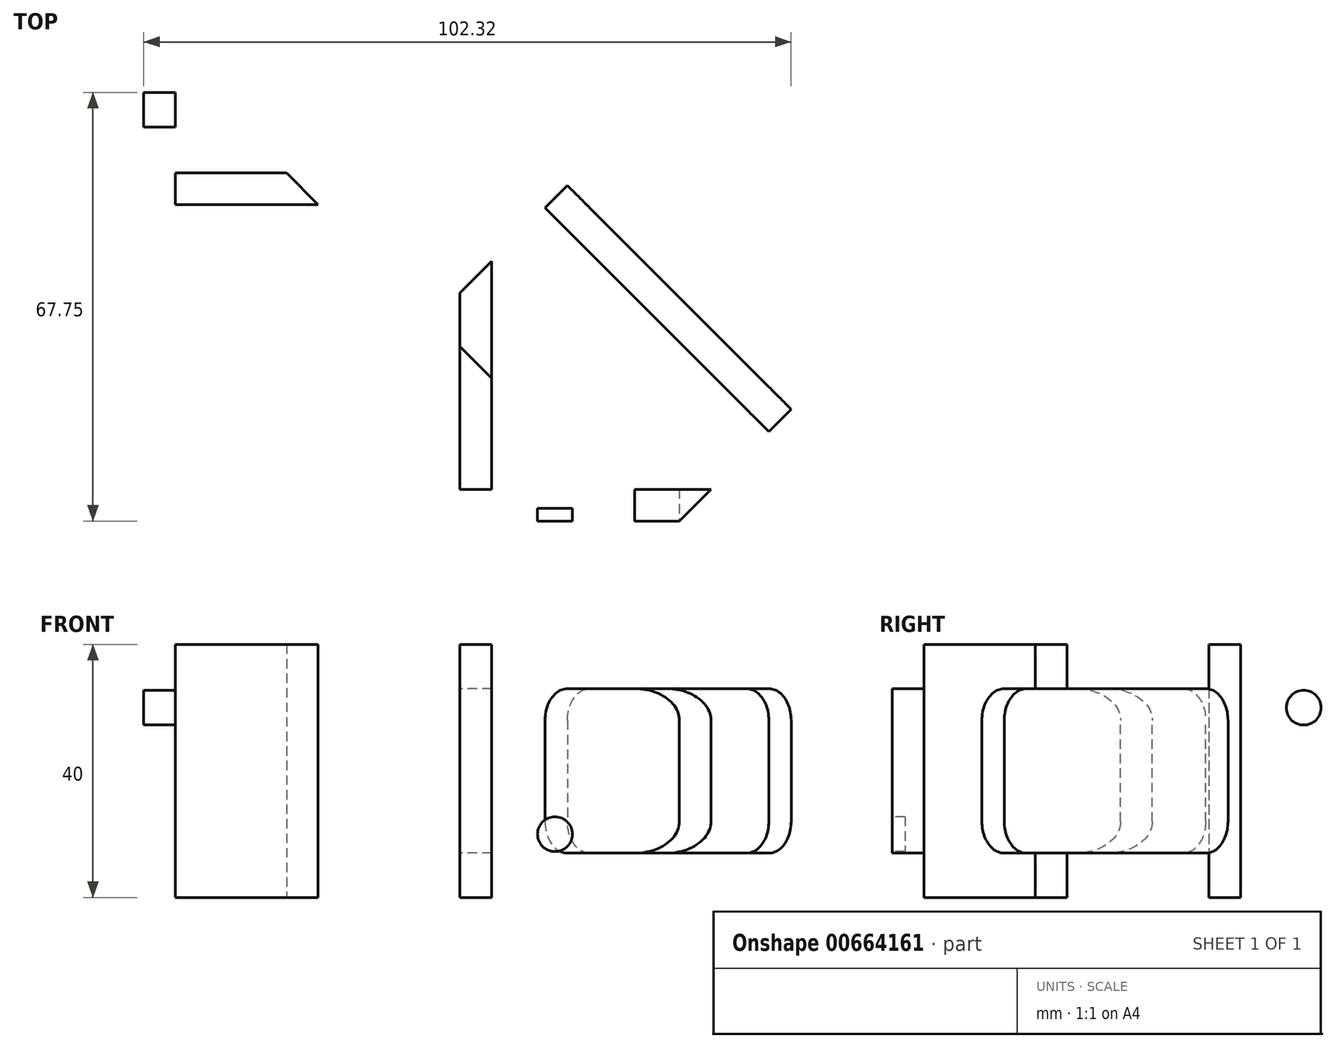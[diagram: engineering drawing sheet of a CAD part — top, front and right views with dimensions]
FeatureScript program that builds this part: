
annotation { "Feature Type Name" : "Feature", "Feature Type Description" : "" }
export const myFeature = defineFeature(function(context is Context, id is Id, definition is map)
    precondition{}
    {
        {
            var Q0;
            Q0=qCreatedBy(makeId("Top.planeOp"),FACE);
            var sketch = newSketch(context, id + "F0", { "sketchPlane" : qUnion([Q0])});
            skLineSegment(sketch, "E0", {"start": v(0, 120) * mm, "end": v(0, 0) * mm});
            skLineSegment(sketch, "E1", {"start": v(0, 0) * mm, "end": v(120, 0) * mm});
            skLineSegment(sketch, "E2", {"start": v(120, 0) * mm, "end": v(0, 120) * mm});
            skLineSegment(sketch, "E3.bottom", {"start": v(0, 0) * mm, "end": v(50, 0) * mm});
            skLineSegment(sketch, "E3.top", {"start": v(0, 50) * mm, "end": v(50, 50) * mm});
            skLineSegment(sketch, "E3.left", {"start": v(0, 0) * mm, "end": v(0, 50) * mm});
            skLineSegment(sketch, "E3.right", {"start": v(50, 0) * mm, "end": v(50, 50) * mm});
            skLineSegment(sketch, "E4", {"start": v(0, 100) * mm, "end": v(100, 0) * mm});
            skLineSegment(sketch, "E5", {"start": v(0, 92.93) * mm, "end": v(42.93, 50) * mm});
            skLineSegment(sketch, "E6", {"start": v(50, 42.93) * mm, "end": v(92.93, 0) * mm});
            skSolve(sketch);
        }
        {
            var Q0;
            {var subQ0=sQuery(id+"F0.wireOp",EDGE,"E0");Q0=makeQuery(id+"F0.imprint","IMPRINT",FACE,{"disambiguationData":[TD([[makeQuery(id+"F0.imprint","IMPRINT",EDGE,{"derivedFrom":subQ0}),1.0]])]});}
            var Q1;
            {var subQ0=sQuery(id+"F0.wireOp",EDGE,"RjJmAIRv-SbMF-DeTt-ittY-7XkKLRqEJTLq");Q1=makeQuery(id+"F0.imprint","IMPRINT",FACE,{"disambiguationData":[TD([[makeQuery(id+"F0.imprint","IMPRINT",EDGE,{"derivedFrom":subQ0}),-1.0]])]});}
            var Q2;
            {var subQ0=sQuery(id+"F0.wireOp",EDGE,"E1");Q2=makeQuery(id+"F0.imprint","IMPRINT",FACE,{"disambiguationData":[TD([[makeQuery(id+"F0.imprint","IMPRINT",EDGE,{"derivedFrom":subQ0}),1.0]])]});}
            var Q3;
            {var subQ3=sQuery(id+"F0.wireOp",EDGE,"E5");Q3=makeQuery(id+"F0.imprint","IMPRINT",FACE,{"disambiguationData":[TD([[makeQuery(id+"F0.imprint","IMPRINT",EDGE,{"derivedFrom":subQ3}),1.0]])]});}
            var Q4;
            {var subQ3=sQuery(id+"F0.wireOp",EDGE,"E6");Q4=makeQuery(id+"F0.imprint","IMPRINT",FACE,{"disambiguationData":[TD([[makeQuery(id+"F0.imprint","IMPRINT",EDGE,{"derivedFrom":subQ3}),1.0]])]});}
            var Q5;
            {var subQ4=sQuery(id+"F0.wireOp",EDGE,"E2");Q5=makeQuery(id+"F0.imprint","IMPRINT",FACE,{"disambiguationData":[TD([[makeQuery(id+"F0.imprint","IMPRINT",EDGE,{"derivedFrom":subQ4}),1.0]])]});}
            extrude(context, id + "F1", {"entities" : qUnion([Q0, Q1, Q2, Q3, Q4, Q5]), "depth" : 40 * mm, "offsetDistance" : 25 * mm});
        }
        {
            var Q0;
            Q0=makeQuery(id+"F1.opExtrude","CAP_FACE",FACE,{"disambiguationData":[OSD([sQuery(id+"F0.wireOp",EDGE,"E0"),sQuery(id+"F0.wireOp",EDGE,"E1"),sQuery(id+"F0.wireOp",EDGE,"E2"),sQuery(id+"F0.wireOp",EDGE,"E3.top"),sQuery(id+"F0.wireOp",EDGE,"E3.right")])],"isStart":false});
            var Q1;
            Q1=makeQuery(id+"F1.opExtrude","CAP_FACE",FACE,{"disambiguationData":[OSD([sQuery(id+"F0.wireOp",EDGE,"E0"),sQuery(id+"F0.wireOp",EDGE,"E1"),sQuery(id+"F0.wireOp",EDGE,"E2"),sQuery(id+"F0.wireOp",EDGE,"E3.top"),sQuery(id+"F0.wireOp",EDGE,"E3.right")])],"isStart":true});
            shell(context, id + "F2", {"entities" : qUnion([Q0, Q1]), "thickness" : 5 * mm});
        }
        {
            var Q0;
            Q0=makeQuery(id+"F1.opExtrude","SWEPT_FACE",FACE,{"disambiguationData":[OSD([sQuery(id+"F0.wireOp",EDGE,"E2")])]});
            var sketch = newSketch(context, id + "F3", { "sketchPlane" : qUnion([Q0])});
            skLineSegment(sketch, "E7.bottom", {"start": v(54.85, 33) * mm, "end": v(14.85, 33) * mm});
            skLineSegment(sketch, "E7.top", {"start": v(54.85, 7) * mm, "end": v(14.85, 7) * mm});
            skLineSegment(sketch, "E7.left", {"start": v(59.85, 28) * mm, "end": v(59.85, 12) * mm});
            skLineSegment(sketch, "E7.right", {"start": v(9.85, 28) * mm, "end": v(9.85, 12) * mm});
            skPoint(sketch, "E8.visualSharp", {"position": v(9.85, 33) * mm});
            skArc(sketch, "E8.filletArc", {"start": v(14.85, 33) * mm, "mid": v(11.32, 31.54) * mm, "end": v(9.85, 28) * mm});
            skPoint(sketch, "E9.visualSharp", {"position": v(9.85, 7) * mm});
            skArc(sketch, "E9.filletArc", {"start": v(9.85, 12) * mm, "mid": v(11.32, 8.46) * mm, "end": v(14.85, 7) * mm});
            skPoint(sketch, "E10.visualSharp", {"position": v(59.85, 33) * mm});
            skArc(sketch, "E10.filletArc", {"start": v(59.85, 28) * mm, "mid": v(58.39, 31.54) * mm, "end": v(54.85, 33) * mm});
            skPoint(sketch, "E11.visualSharp", {"position": v(59.85, 7) * mm});
            skArc(sketch, "E11.filletArc", {"start": v(54.85, 7) * mm, "mid": v(58.39, 8.46) * mm, "end": v(59.85, 12) * mm});
            skLineSegment(sketch, "E12", {"start": v(0, 40) * mm, "end": v(0, 0) * mm, "construction": true});
            skArc(sketch, "E13.MirrorCS", {"start": v(-59.85, 28) * mm, "mid": v(-58.39, 31.54) * mm, "end": v(-54.85, 33) * mm});
            skArc(sketch, "E14.MirrorCS", {"start": v(-54.85, 7) * mm, "mid": v(-58.39, 8.46) * mm, "end": v(-59.85, 12) * mm});
            skLineSegment(sketch, "E15.MirrorCS", {"start": v(-59.85, 28) * mm, "end": v(-59.85, 12) * mm});
            skPoint(sketch, "E16.MirrorP", {"position": v(-59.85, 7) * mm});
            skPoint(sketch, "E17.MirrorP", {"position": v(-59.85, 33) * mm});
            skArc(sketch, "E18.MirrorCS", {"start": v(-14.85, 33) * mm, "mid": v(-11.32, 31.54) * mm, "end": v(-9.85, 28) * mm});
            skPoint(sketch, "E19.MirrorP", {"position": v(-9.85, 33) * mm});
            skArc(sketch, "E20.MirrorCS", {"start": v(-9.85, 12) * mm, "mid": v(-11.32, 8.46) * mm, "end": v(-14.85, 7) * mm});
            skLineSegment(sketch, "E21.MirrorCS", {"start": v(-54.85, 33) * mm, "end": v(-14.85, 33) * mm});
            skLineSegment(sketch, "E22.MirrorCS", {"start": v(-54.85, 7) * mm, "end": v(-14.85, 7) * mm});
            skLineSegment(sketch, "E23.MirrorCS", {"start": v(-9.85, 28) * mm, "end": v(-9.85, 12) * mm});
            skPoint(sketch, "E24.MirrorP", {"position": v(-9.85, 7) * mm});
            skSolve(sketch);
        }
        {
            var Q0;
            Q0=makeQuery(id+"F3.imprint","IMPRINT",FACE,{"disambiguationData":[TD([[makeQuery(id+"F3.imprint","IMPRINT",EDGE,{"derivedFrom":sQuery(id+"F3.wireOp",EDGE,"E7.bottom")}),1.0]])]});
            var Q1;
            Q1=makeQuery(id+"F3.imprint","IMPRINT",FACE,{"disambiguationData":[TD([[makeQuery(id+"F3.imprint","IMPRINT",EDGE,{"derivedFrom":sQuery(id+"F3.wireOp",EDGE,"E14.MirrorCS")}),-1.0]])]});
            extrude(context, id + "F4", {"entities" : qUnion([Q0, Q1]), "operationType" : NewBodyOperationType.REMOVE, "oppositeDirection" : true, "depth" : 30 * mm, "offsetDistance" : 25 * mm});
        }
        {
            var Q0;
            Q0=makeQuery(id+"F1.opExtrude","SWEPT_FACE",FACE,{"disambiguationData":[OSD([sQuery(id+"F0.wireOp",EDGE,"E0")])]});
            var sketch = newSketch(context, id + "F5", { "sketchPlane" : qUnion([Q0])});
            skCircle(sketch, "E25", {"center": v(-95, 10) * mm, "radius": 2.75 * mm});
            skCircle(sketch, "E26", {"center": v(-65, 10) * mm, "radius": 2.75 * mm});
            skLineSegment(sketch, "E27", {"start": v(-120, 20) * mm, "end": v(-50, 20) * mm, "construction": true});
            skCircle(sketch, "E28.MirrorC", {"center": v(-95, 30) * mm, "radius": 2.75 * mm});
            skCircle(sketch, "E29.MirrorC", {"center": v(-65, 30) * mm, "radius": 2.75 * mm});
            skSolve(sketch);
        }
        {
            var Q0;
            Q0=makeQuery(id+"F5.imprint","IMPRINT",FACE,{"disambiguationData":[TD([[makeQuery(id+"F5.imprint","IMPRINT",EDGE,{"derivedFrom":sQuery(id+"F5.wireOp",EDGE,"E25")}),1.0]])]});
            var Q1;
            Q1=makeQuery(id+"F5.imprint","IMPRINT",FACE,{"disambiguationData":[TD([[makeQuery(id+"F5.imprint","IMPRINT",EDGE,{"derivedFrom":sQuery(id+"F5.wireOp",EDGE,"E28.MirrorC")}),-1.0]])]});
            var Q2;
            Q2=makeQuery(id+"F5.imprint","IMPRINT",FACE,{"disambiguationData":[TD([[makeQuery(id+"F5.imprint","IMPRINT",EDGE,{"derivedFrom":sQuery(id+"F5.wireOp",EDGE,"E26")}),1.0]])]});
            var Q3;
            Q3=makeQuery(id+"F5.imprint","IMPRINT",FACE,{"disambiguationData":[TD([[makeQuery(id+"F5.imprint","IMPRINT",EDGE,{"derivedFrom":sQuery(id+"F5.wireOp",EDGE,"E29.MirrorC")}),-1.0]])]});
            var Q4;
            Q4=makeQuery(id+"F2.opShell","OFFSET_FACE",FACE,{"disambiguationData":[OSD([sQuery(id+"F0.wireOp",EDGE,"E0")])]});
            extrude(context, id + "F6", {"entities" : qUnion([Q0, Q1, Q2, Q3]), "operationType" : NewBodyOperationType.REMOVE, "endBound" : BoundingType.UP_TO_SURFACE, "oppositeDirection" : true, "depth" : 25 * mm, "endBoundEntityFace" : qUnion([Q4]), "offsetDistance" : 25 * mm});
        }
        {
            var Q0;
            Q0=makeQuery(id+"F1.opExtrude","SWEPT_FACE",FACE,{"disambiguationData":[OSD([sQuery(id+"F0.wireOp",EDGE,"E1")])]});
            var sketch = newSketch(context, id + "F7", { "sketchPlane" : qUnion([Q0])});
            skLineSegment(sketch, "E30", {"start": v(120, 20) * mm, "end": v(50, 20) * mm, "construction": true});
            skCircle(sketch, "E31", {"center": v(95, 30) * mm, "radius": 2.75 * mm});
            skCircle(sketch, "E32", {"center": v(65, 30) * mm, "radius": 2.75 * mm});
            skCircle(sketch, "E33.MirrorC", {"center": v(95, 10) * mm, "radius": 2.75 * mm});
            skCircle(sketch, "E34.MirrorC", {"center": v(65, 10) * mm, "radius": 2.75 * mm});
            skSolve(sketch);
        }
        {
            var Q0;
            Q0=makeQuery(id+"F7.imprint","IMPRINT",FACE,{"disambiguationData":[TD([[makeQuery(id+"F7.imprint","IMPRINT",EDGE,{"derivedFrom":sQuery(id+"F7.wireOp",EDGE,"E32")}),1.0]])]});
            var Q1;
            Q1=makeQuery(id+"F7.imprint","IMPRINT",FACE,{"disambiguationData":[TD([[makeQuery(id+"F7.imprint","IMPRINT",EDGE,{"derivedFrom":sQuery(id+"F7.wireOp",EDGE,"E31")}),1.0]])]});
            var Q2;
            Q2=makeQuery(id+"F7.imprint","IMPRINT",FACE,{"disambiguationData":[TD([[makeQuery(id+"F7.imprint","IMPRINT",EDGE,{"derivedFrom":sQuery(id+"F7.wireOp",EDGE,"E33.MirrorC")}),-1.0]])]});
            var Q3;
            Q3=makeQuery(id+"F7.imprint","IMPRINT",FACE,{"disambiguationData":[TD([[makeQuery(id+"F7.imprint","IMPRINT",EDGE,{"derivedFrom":sQuery(id+"F7.wireOp",EDGE,"E34.MirrorC")}),-1.0]])]});
            var Q4;
            Q4=makeQuery(id+"F2.opShell","OFFSET_FACE",FACE,{"disambiguationData":[OSD([sQuery(id+"F0.wireOp",EDGE,"E1")])]});
            extrude(context, id + "F8", {"entities" : qUnion([Q0, Q1, Q2, Q3]), "operationType" : NewBodyOperationType.REMOVE, "endBound" : BoundingType.UP_TO_SURFACE, "oppositeDirection" : true, "depth" : 25 * mm, "endBoundEntityFace" : qUnion([Q4]), "offsetDistance" : 25 * mm});
        }
        {
            var Q0;
            Q0=makeQuery(id+"F2.opShell","OFFSET_FACE",FACE,{"disambiguationData":[OSD([sQuery(id+"F0.wireOp",EDGE,"E0")])]});
            var sketch = newSketch(context, id + "F9", { "sketchPlane" : qUnion([Q0])});
            skCircle(sketch, "E35.cCircle", {"center": v(65, 30) * mm, "radius": 3.85 * mm, "construction": true});
            skLineSegment(sketch, "E35.0", {"start": v(65, 25.55) * mm, "end": v(61.15, 27.78) * mm});
            skLineSegment(sketch, "E35.1", {"start": v(61.15, 27.78) * mm, "end": v(61.15, 32.22) * mm});
            skLineSegment(sketch, "E35.2", {"start": v(61.15, 32.22) * mm, "end": v(65, 34.45) * mm});
            skLineSegment(sketch, "E35.3", {"start": v(65, 34.45) * mm, "end": v(68.85, 32.22) * mm});
            skLineSegment(sketch, "E35.4", {"start": v(68.85, 32.22) * mm, "end": v(68.85, 27.78) * mm});
            skLineSegment(sketch, "E35.5", {"start": v(68.85, 27.78) * mm, "end": v(65, 25.55) * mm});
            skPoint(sketch, "E35.0.midPoint", {"position": v(63.08, 26.67) * mm});
            skCircle(sketch, "E36.cCircle", {"center": v(65, 10) * mm, "radius": 3.85 * mm, "construction": true});
            skLineSegment(sketch, "E36.0", {"start": v(61.15, 7.78) * mm, "end": v(61.15, 12.22) * mm});
            skLineSegment(sketch, "E36.1", {"start": v(61.15, 12.22) * mm, "end": v(65, 14.45) * mm});
            skLineSegment(sketch, "E36.2", {"start": v(65, 14.45) * mm, "end": v(68.85, 12.22) * mm});
            skLineSegment(sketch, "E36.3", {"start": v(68.85, 12.22) * mm, "end": v(68.85, 7.78) * mm});
            skLineSegment(sketch, "E36.4", {"start": v(68.85, 7.78) * mm, "end": v(65, 5.55) * mm});
            skLineSegment(sketch, "E36.5", {"start": v(65, 5.55) * mm, "end": v(61.15, 7.78) * mm});
            skPoint(sketch, "E36.0.midPoint", {"position": v(61.15, 10) * mm});
            skCircle(sketch, "E37.cCircle", {"center": v(95, 30) * mm, "radius": 3.85 * mm, "construction": true});
            skLineSegment(sketch, "E37.0", {"start": v(95, 25.55) * mm, "end": v(91.15, 27.78) * mm});
            skLineSegment(sketch, "E37.1", {"start": v(91.15, 27.78) * mm, "end": v(91.15, 32.22) * mm});
            skLineSegment(sketch, "E37.2", {"start": v(91.15, 32.22) * mm, "end": v(95, 34.45) * mm});
            skLineSegment(sketch, "E37.3", {"start": v(95, 34.45) * mm, "end": v(98.85, 32.22) * mm});
            skLineSegment(sketch, "E37.4", {"start": v(98.85, 32.22) * mm, "end": v(98.85, 27.78) * mm});
            skLineSegment(sketch, "E37.5", {"start": v(98.85, 27.78) * mm, "end": v(95, 25.55) * mm});
            skPoint(sketch, "E37.0.midPoint", {"position": v(93.07, 26.67) * mm});
            skCircle(sketch, "E38.cCircle", {"center": v(95, 10) * mm, "radius": 3.85 * mm, "construction": true});
            skLineSegment(sketch, "E38.0", {"start": v(95, 5.55) * mm, "end": v(91.15, 7.78) * mm});
            skLineSegment(sketch, "E38.1", {"start": v(91.15, 7.78) * mm, "end": v(91.15, 12.22) * mm});
            skLineSegment(sketch, "E38.2", {"start": v(91.15, 12.22) * mm, "end": v(95, 14.45) * mm});
            skLineSegment(sketch, "E38.3", {"start": v(95, 14.45) * mm, "end": v(98.85, 12.22) * mm});
            skLineSegment(sketch, "E38.4", {"start": v(98.85, 12.22) * mm, "end": v(98.85, 7.78) * mm});
            skLineSegment(sketch, "E38.5", {"start": v(98.85, 7.78) * mm, "end": v(95, 5.55) * mm});
            skPoint(sketch, "E38.0.midPoint", {"position": v(93.08, 6.67) * mm});
            skSolve(sketch);
        }
        {
            var Q0;
            Q0=makeQuery(id+"F9.imprint","IMPRINT",FACE,{"disambiguationData":[TD([[makeQuery(id+"F9.imprint","IMPRINT",EDGE,{"derivedFrom":sQuery(id+"F9.wireOp",EDGE,"E35.0")}),-1.0]])]});
            var Q1;
            Q1=makeQuery(id+"F9.imprint","IMPRINT",FACE,{"disambiguationData":[TD([[makeQuery(id+"F9.imprint","IMPRINT",EDGE,{"derivedFrom":sQuery(id+"F9.wireOp",EDGE,"E36.0")}),-1.0]])]});
            var Q2;
            Q2=makeQuery(id+"F9.imprint","IMPRINT",FACE,{"disambiguationData":[TD([[makeQuery(id+"F9.imprint","IMPRINT",EDGE,{"derivedFrom":sQuery(id+"F9.wireOp",EDGE,"E38.0")}),-1.0]])]});
            var Q3;
            Q3=makeQuery(id+"F9.imprint","IMPRINT",FACE,{"disambiguationData":[TD([[makeQuery(id+"F9.imprint","IMPRINT",EDGE,{"derivedFrom":sQuery(id+"F9.wireOp",EDGE,"E37.0")}),-1.0]])]});
            extrude(context, id + "F10", {"entities" : qUnion([Q0, Q1, Q2, Q3]), "operationType" : NewBodyOperationType.REMOVE, "oppositeDirection" : true, "depth" : 3 * mm, "offsetDistance" : 25 * mm});
        }
        {
            var Q0;
            Q0=makeQuery(id+"F2.opShell","OFFSET_FACE",FACE,{"disambiguationData":[OSD([sQuery(id+"F0.wireOp",EDGE,"E1")])]});
            var sketch = newSketch(context, id + "F11", { "sketchPlane" : qUnion([Q0])});
            skCircle(sketch, "E39.cCircle", {"center": v(-95, 30) * mm, "radius": 3.85 * mm, "construction": true});
            skLineSegment(sketch, "E39.0", {"start": v(-95, 34.45) * mm, "end": v(-91.15, 32.22) * mm});
            skLineSegment(sketch, "E39.1", {"start": v(-91.15, 32.22) * mm, "end": v(-91.15, 27.78) * mm});
            skLineSegment(sketch, "E39.2", {"start": v(-91.15, 27.78) * mm, "end": v(-95, 25.55) * mm});
            skLineSegment(sketch, "E39.3", {"start": v(-95, 25.55) * mm, "end": v(-98.85, 27.78) * mm});
            skLineSegment(sketch, "E39.4", {"start": v(-98.85, 27.78) * mm, "end": v(-98.85, 32.22) * mm});
            skLineSegment(sketch, "E39.5", {"start": v(-98.85, 32.22) * mm, "end": v(-95, 34.45) * mm});
            skPoint(sketch, "E39.0.midPoint", {"position": v(-93.07, 33.33) * mm});
            skCircle(sketch, "E40.cCircle", {"center": v(-95, 10) * mm, "radius": 3.85 * mm, "construction": true});
            skLineSegment(sketch, "E40.0", {"start": v(-95, 14.45) * mm, "end": v(-91.15, 12.22) * mm});
            skLineSegment(sketch, "E40.1", {"start": v(-91.15, 12.22) * mm, "end": v(-91.15, 7.78) * mm});
            skLineSegment(sketch, "E40.2", {"start": v(-91.15, 7.78) * mm, "end": v(-95, 5.55) * mm});
            skLineSegment(sketch, "E40.3", {"start": v(-95, 5.55) * mm, "end": v(-98.85, 7.78) * mm});
            skLineSegment(sketch, "E40.4", {"start": v(-98.85, 7.78) * mm, "end": v(-98.85, 12.22) * mm});
            skLineSegment(sketch, "E40.5", {"start": v(-98.85, 12.22) * mm, "end": v(-95, 14.45) * mm});
            skPoint(sketch, "E40.0.midPoint", {"position": v(-93.07, 13.33) * mm});
            skCircle(sketch, "E41.cCircle", {"center": v(-65, 10) * mm, "radius": 3.85 * mm, "construction": true});
            skLineSegment(sketch, "E41.0", {"start": v(-65, 14.45) * mm, "end": v(-61.15, 12.22) * mm});
            skLineSegment(sketch, "E41.1", {"start": v(-61.15, 12.22) * mm, "end": v(-61.15, 7.78) * mm});
            skLineSegment(sketch, "E41.2", {"start": v(-61.15, 7.78) * mm, "end": v(-65, 5.55) * mm});
            skLineSegment(sketch, "E41.3", {"start": v(-65, 5.55) * mm, "end": v(-68.85, 7.78) * mm});
            skLineSegment(sketch, "E41.4", {"start": v(-68.85, 7.78) * mm, "end": v(-68.85, 12.22) * mm});
            skLineSegment(sketch, "E41.5", {"start": v(-68.85, 12.22) * mm, "end": v(-65, 14.45) * mm});
            skPoint(sketch, "E41.0.midPoint", {"position": v(-63.07, 13.33) * mm});
            skCircle(sketch, "E42.cCircle", {"center": v(-65, 30) * mm, "radius": 3.85 * mm, "construction": true});
            skLineSegment(sketch, "E42.0", {"start": v(-65, 34.45) * mm, "end": v(-61.15, 32.22) * mm});
            skLineSegment(sketch, "E42.1", {"start": v(-61.15, 32.22) * mm, "end": v(-61.15, 27.78) * mm});
            skLineSegment(sketch, "E42.2", {"start": v(-61.15, 27.78) * mm, "end": v(-65, 25.55) * mm});
            skLineSegment(sketch, "E42.3", {"start": v(-65, 25.55) * mm, "end": v(-68.85, 27.78) * mm});
            skLineSegment(sketch, "E42.4", {"start": v(-68.85, 27.78) * mm, "end": v(-68.85, 32.22) * mm});
            skLineSegment(sketch, "E42.5", {"start": v(-68.85, 32.22) * mm, "end": v(-65, 34.45) * mm});
            skPoint(sketch, "E42.0.midPoint", {"position": v(-63.07, 33.33) * mm});
            skSolve(sketch);
        }
        {
            var Q0;
            Q0=makeQuery(id+"F11.imprint","IMPRINT",FACE,{"disambiguationData":[TD([[makeQuery(id+"F11.imprint","IMPRINT",EDGE,{"derivedFrom":sQuery(id+"F11.wireOp",EDGE,"E40.0")}),-1.0]])]});
            var Q1;
            Q1=makeQuery(id+"F11.imprint","IMPRINT",FACE,{"disambiguationData":[TD([[makeQuery(id+"F11.imprint","IMPRINT",EDGE,{"derivedFrom":sQuery(id+"F11.wireOp",EDGE,"E39.0")}),-1.0]])]});
            var Q2;
            Q2=makeQuery(id+"F11.imprint","IMPRINT",FACE,{"disambiguationData":[TD([[makeQuery(id+"F11.imprint","IMPRINT",EDGE,{"derivedFrom":sQuery(id+"F11.wireOp",EDGE,"E42.0")}),-1.0]])]});
            var Q3;
            Q3=makeQuery(id+"F11.imprint","IMPRINT",FACE,{"disambiguationData":[TD([[makeQuery(id+"F11.imprint","IMPRINT",EDGE,{"derivedFrom":sQuery(id+"F11.wireOp",EDGE,"E41.0")}),-1.0]])]});
            extrude(context, id + "F12", {"entities" : qUnion([Q0, Q1, Q2, Q3]), "operationType" : NewBodyOperationType.REMOVE, "oppositeDirection" : true, "depth" : 3 * mm, "offsetDistance" : 25 * mm});
        }
    });
